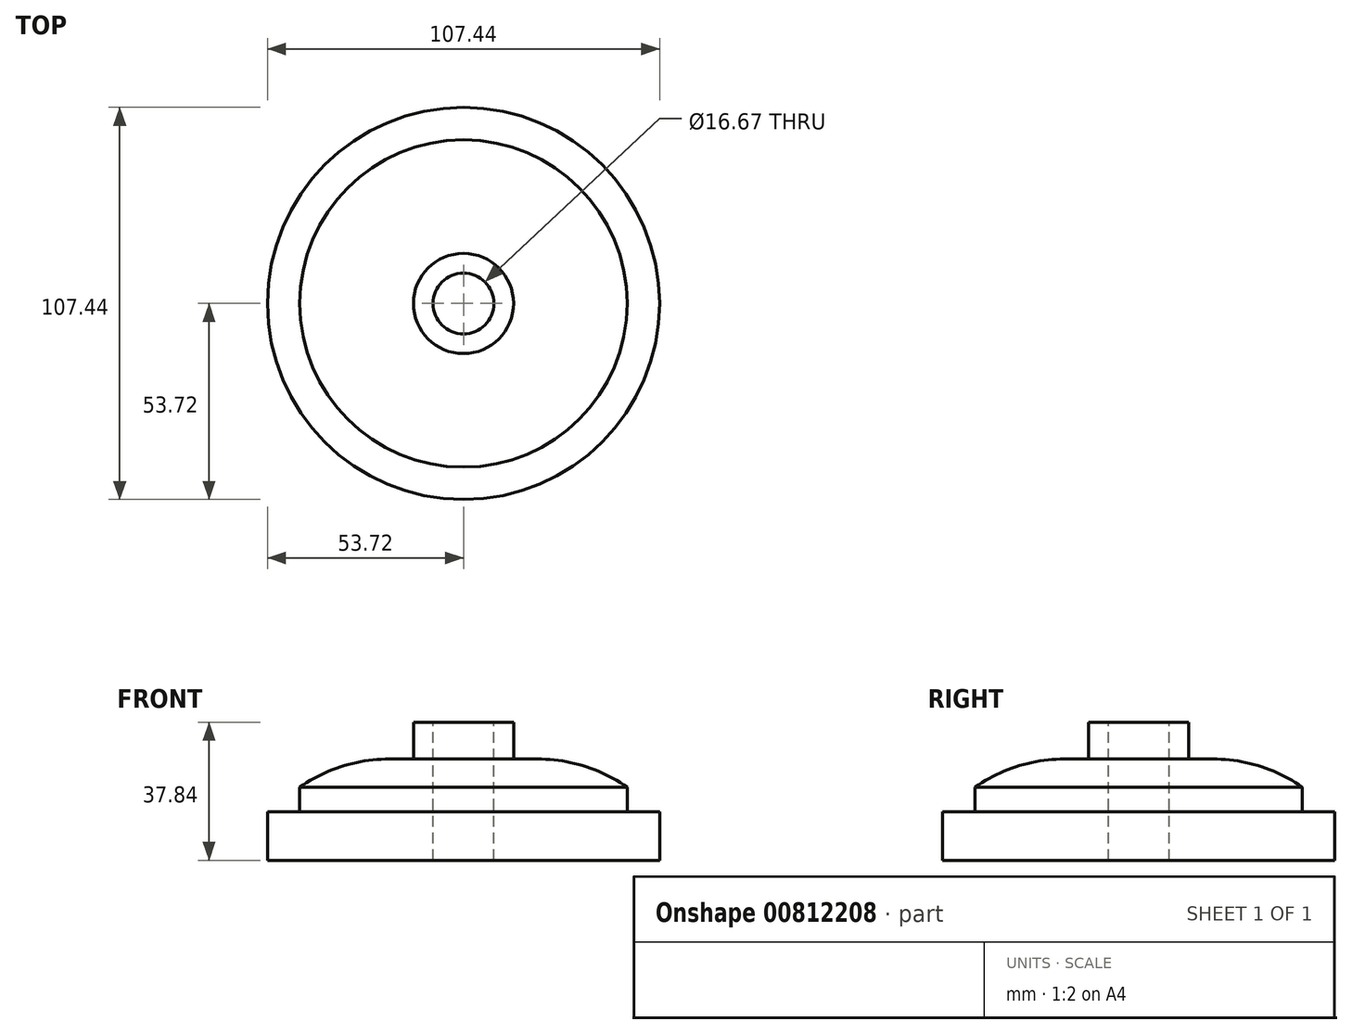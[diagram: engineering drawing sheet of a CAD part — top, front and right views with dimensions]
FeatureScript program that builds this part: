
annotation { "Feature Type Name" : "Feature", "Feature Type Description" : "" }
export const myFeature = defineFeature(function(context is Context, id is Id, definition is map)
    precondition{}
    {
        {
            var Q0;
            Q0=qCreatedBy(makeId("Front.planeOp"),FACE);
            var sketch = newSketch(context, id + "F0", { "sketchPlane" : qUnion([Q0])});
            skLineSegment(sketch, "E0", {"start": v(-53.72, -6.73) * mm, "end": v(-53.72, -20.06) * mm});
            skLineSegment(sketch, "E1", {"start": v(-53.72, -20.06) * mm, "end": v(0, -20.06) * mm});
            skLineSegment(sketch, "E2", {"start": v(0, -20.06) * mm, "end": v(0, 17.78) * mm});
            skLineSegment(sketch, "E3", {"start": v(0, 17.78) * mm, "end": v(-13.72, 17.78) * mm});
            skLineSegment(sketch, "E4", {"start": v(-13.72, 17.78) * mm, "end": v(-13.72, 7.68) * mm});
            skLineSegment(sketch, "E5", {"start": v(-44.83, 0) * mm, "end": v(-44.83, -6.73) * mm});
            skLineSegment(sketch, "E6", {"start": v(-44.83, -6.73) * mm, "end": v(-53.72, -6.73) * mm});
            skLineSegment(sketch, "E7", {"start": v(-13.72, 7.68) * mm, "end": v(-20.32, 7.68) * mm});
            skArc(sketch, "E8", {"start": v(-20.32, 7.68) * mm, "mid": v(-33.16, 5.71) * mm, "end": v(-44.83, 0) * mm});
            skSolve(sketch);
        }
        {
            var Q0;
            Q0=makeQuery(id+"F0.imprint","IMPRINT",FACE,{"disambiguationData":[TD([[makeQuery(id+"F0.imprint","IMPRINT",EDGE,{"derivedFrom":sQuery(id+"F0.wireOp",EDGE,"E0")}),1.0]])]});
            var Q1;
            Q1=sQuery(id+"F0.wireOp",EDGE,"E2");
            revolve(context, id + "F1", {"surfaceOperationType" : NewSurfaceOperationType.NEW, "entities" : qUnion([Q0]), "axis" : qUnion([Q1]), "revolveType" : RevolveType.FULL});
        }
        {
            var Q0;
            Q0=makeQuery(id+"F1.opRevolve","SWEPT_FACE",FACE,{"disambiguationData":[OSD([sQuery(id+"F0.wireOp",EDGE,"E3")])]});
            var sketch = newSketch(context, id + "F2", { "sketchPlane" : qUnion([Q0])});
            skCircle(sketch, "E9", {"center": v(0, 0) * mm, "radius": 9.53 * mm});
            skSolve(sketch);
        }
        {
            var Q0;
            Q0=sQuery(id+"F2.wireOp",VERTEX,"E9.center");
            var Q1;
            Q1=makeQuery(id+"F1.opRevolve","SWEPT_BODY",BODY,{"disambiguationData":[OSD([sQuery(id+"F0.wireOp",EDGE,"E0"),sQuery(id+"F0.wireOp",EDGE,"E1"),sQuery(id+"F0.wireOp",EDGE,"E2"),sQuery(id+"F0.wireOp",EDGE,"E3"),sQuery(id+"F0.wireOp",EDGE,"E4"),sQuery(id+"F0.wireOp",EDGE,"E5"),sQuery(id+"F0.wireOp",EDGE,"E6"),sQuery(id+"F0.wireOp",EDGE,"E7"),sQuery(id+"F0.wireOp",EDGE,"E8")])]});
            hole(context, id + "F3", {"style" : HoleStyle.SIMPLE, "endStyle" : HoleEndStyle.THROUGH, "standardTappedOrClearance" : lookupTablePath({ "standard" : "ANSI", "engagement" : "75%", "pitch" : "10 tpi", "size" : "3/4", "type" : "Tapped" }), "standardBlindInLast" : lookupTablePath({ "standard" : "ANSI", "engagement" : "75%", "pitch" : "10 tpi", "size" : "3/4", "type" : "Tapped" }), "holeDiameter" : 16.67 * mm, "majorDiameter" : 19.05 * mm, "showTappedDepth" : true, "isTappedThrough" : true, "tappedDepth" : 12.7 * mm, "tapClearance" : 3, "locations" : qUnion([Q0]), "scope" : qUnion([Q1])});
        }
    });
